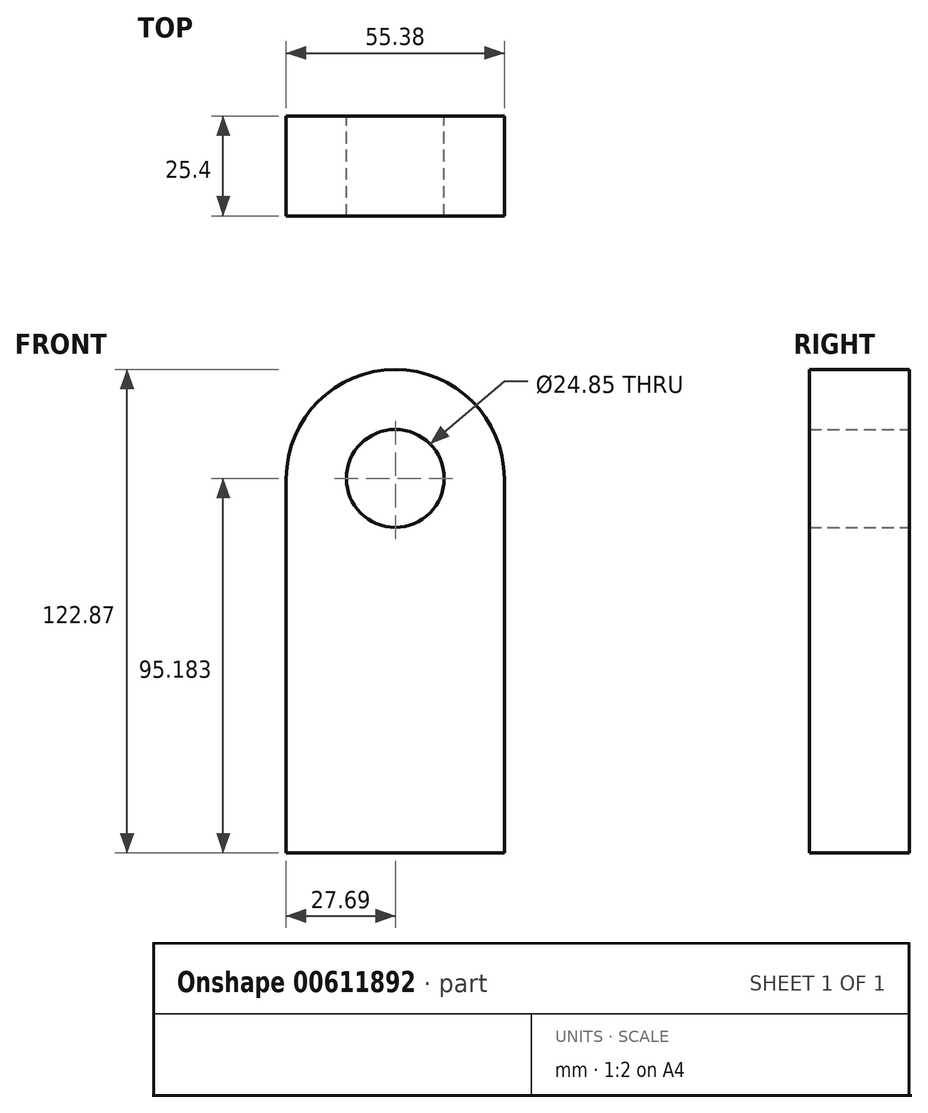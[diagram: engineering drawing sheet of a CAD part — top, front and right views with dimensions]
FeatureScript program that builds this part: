
annotation { "Feature Type Name" : "Feature", "Feature Type Description" : "" }
export const myFeature = defineFeature(function(context is Context, id is Id, definition is map)
    precondition{}
    {
        {
            var Q0;
            Q0=qCreatedBy(makeId("Front.planeOp"),FACE);
            var sketch = newSketch(context, id + "F0", { "sketchPlane" : qUnion([Q0])});
            skLineSegment(sketch, "E0.bottom", {"start": v(27.69, -47.6) * mm, "end": v(-27.69, -47.6) * mm});
            skLineSegment(sketch, "E0.left", {"start": v(27.69, -47.6) * mm, "end": v(27.69, 47.6) * mm});
            skLineSegment(sketch, "E0.right", {"start": v(-27.69, -47.6) * mm, "end": v(-27.69, 47.6) * mm});
            skPoint(sketch, "E0.middle", {"position": v(0, 0) * mm});
            skArc(sketch, "E1", {"start": v(27.69, 47.6) * mm, "mid": v(0, 75.28) * mm, "end": v(-27.69, 47.6) * mm});
            skCircle(sketch, "E2", {"center": v(0, 47.6) * mm, "radius": 12.43 * mm});
            skSolve(sketch);
        }
        {
            var Q0;
            Q0 = qSketchRegion(id + "F0", true);
            extrude(context, id + "F1", {"entities" : qUnion([Q0]), "depth" : 25.4 * mm, "offsetDistance" : 25.4 * mm});
        }
    });
